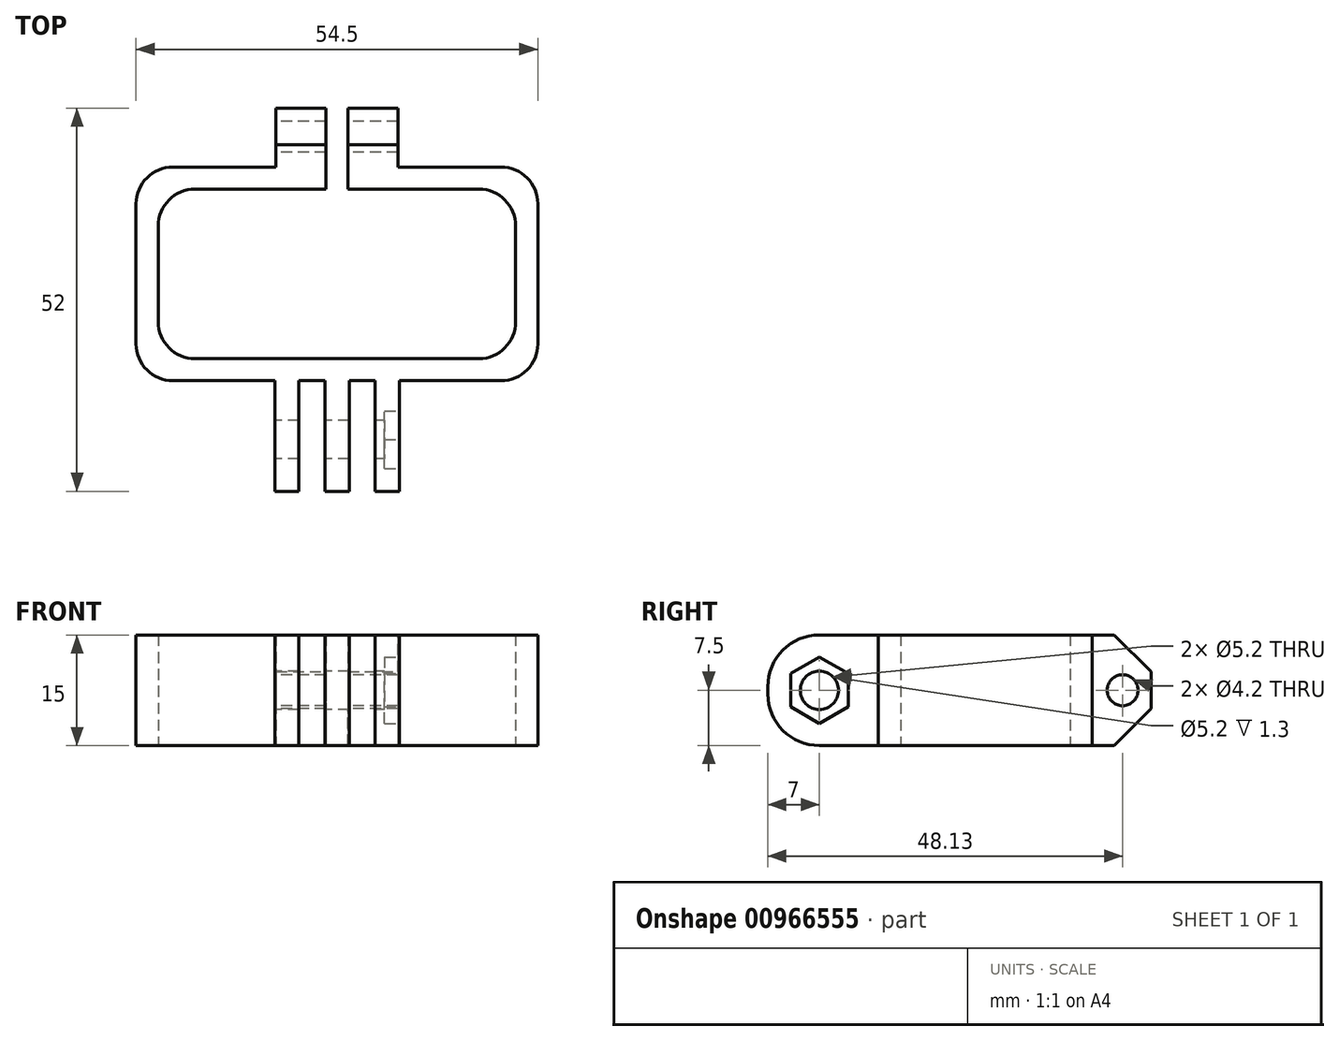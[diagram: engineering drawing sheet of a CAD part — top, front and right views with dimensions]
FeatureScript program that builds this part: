
annotation { "Feature Type Name" : "Feature", "Feature Type Description" : "" }
export const myFeature = defineFeature(function(context is Context, id is Id, definition is map)
    precondition{}
    {
        {
            var Q0;
            Q0=qCreatedBy(makeId("Top.planeOp"),FACE);
            var sketch = newSketch(context, id + "F0", { "sketchPlane" : qUnion([Q0])});
            skLineSegment(sketch, "E0.bottom", {"start": v(22.25, -14.5) * mm, "end": v(8.45, -14.5) * mm});
            skLineSegment(sketch, "E0.top", {"start": v(22.25, 14.5) * mm, "end": v(8.28, 14.5) * mm});
            skLineSegment(sketch, "E0.left", {"start": v(27.25, -9.5) * mm, "end": v(27.25, 9.5) * mm});
            skLineSegment(sketch, "E0.right", {"start": v(-27.25, -9.5) * mm, "end": v(-27.25, 9.5) * mm});
            skPoint(sketch, "E0.middle", {"position": v(0, 0) * mm});
            skLineSegment(sketch, "E1.top", {"start": v(-8.45, -29.5) * mm, "end": v(-5.15, -29.5) * mm});
            skLineSegment(sketch, "E1.left", {"start": v(-8.45, -14.5) * mm, "end": v(-8.45, -29.5) * mm});
            skLineSegment(sketch, "E1.right", {"start": v(-5.15, -14.5) * mm, "end": v(-5.15, -29.5) * mm});
            skLineSegment(sketch, "E2.top", {"start": v(-1.65, -29.5) * mm, "end": v(1.65, -29.5) * mm});
            skLineSegment(sketch, "E2.left", {"start": v(-1.65, -14.5) * mm, "end": v(-1.65, -29.5) * mm});
            skLineSegment(sketch, "E2.right", {"start": v(1.65, -14.5) * mm, "end": v(1.65, -29.5) * mm});
            skLineSegment(sketch, "E3.top", {"start": v(5.15, -29.5) * mm, "end": v(8.45, -29.5) * mm});
            skLineSegment(sketch, "E3.left", {"start": v(5.15, -14.5) * mm, "end": v(5.15, -29.5) * mm});
            skLineSegment(sketch, "E3.right", {"start": v(8.45, -14.5) * mm, "end": v(8.45, -29.5) * mm});
            skLineSegment(sketch, "E4", {"start": v(-5.15, -22.9) * mm, "end": v(-1.65, -22.9) * mm, "construction": true});
            skLineSegment(sketch, "E5", {"start": v(1.65, -22.9) * mm, "end": v(5.15, -22.9) * mm, "construction": true});
            skLineSegment(sketch, "E6.bottom", {"start": v(19.25, -11.5) * mm, "end": v(-19.25, -11.5) * mm});
            skLineSegment(sketch, "E6.top", {"start": v(19.25, 11.5) * mm, "end": v(1.5, 11.5) * mm});
            skLineSegment(sketch, "E6.left", {"start": v(24.25, -6.5) * mm, "end": v(24.25, 6.5) * mm});
            skLineSegment(sketch, "E6.right", {"start": v(-24.25, -6.5) * mm, "end": v(-24.25, 6.5) * mm});
            skLineSegment(sketch, "E7", {"start": v(-1.65, -14.5) * mm, "end": v(1.65, -29.5) * mm, "construction": true});
            skLineSegment(sketch, "E8", {"start": v(1.65, -14.5) * mm, "end": v(-1.65, -29.5) * mm, "construction": true});
            skLineSegment(sketch, "E9", {"start": v(0, 57.59) * mm, "end": v(0, -68.32) * mm, "construction": true});
            skLineSegment(sketch, "E10.trimOffspring", {"start": v(-8.45, -14.5) * mm, "end": v(-22.25, -14.5) * mm});
            skLineSegment(sketch, "E11.trimOffspring", {"start": v(-1.65, -14.5) * mm, "end": v(-5.15, -14.5) * mm});
            skLineSegment(sketch, "E12.trimOffspring", {"start": v(5.15, -14.5) * mm, "end": v(1.65, -14.5) * mm});
            skPoint(sketch, "E13.visualSharp", {"position": v(-24.25, 11.5) * mm});
            skArc(sketch, "E13.filletArc", {"start": v(-19.25, 11.5) * mm, "mid": v(-22.79, 10.04) * mm, "end": v(-24.25, 6.5) * mm});
            skPoint(sketch, "E14.visualSharp", {"position": v(24.25, 11.5) * mm});
            skArc(sketch, "E14.filletArc", {"start": v(24.25, 6.5) * mm, "mid": v(22.79, 10.04) * mm, "end": v(19.25, 11.5) * mm});
            skPoint(sketch, "E15.visualSharp", {"position": v(24.25, -11.5) * mm});
            skArc(sketch, "E15.filletArc", {"start": v(19.25, -11.5) * mm, "mid": v(22.79, -10.04) * mm, "end": v(24.25, -6.5) * mm});
            skPoint(sketch, "E16.visualSharp", {"position": v(-24.25, -11.5) * mm});
            skArc(sketch, "E16.filletArc", {"start": v(-24.25, -6.5) * mm, "mid": v(-22.79, -10.04) * mm, "end": v(-19.25, -11.5) * mm});
            skPoint(sketch, "E17.visualSharp", {"position": v(-27.25, -14.5) * mm});
            skArc(sketch, "E17.filletArc", {"start": v(-27.25, -9.5) * mm, "mid": v(-25.79, -13.04) * mm, "end": v(-22.25, -14.5) * mm});
            skPoint(sketch, "E18.visualSharp", {"position": v(-27.25, 14.5) * mm});
            skArc(sketch, "E18.filletArc", {"start": v(-22.25, 14.5) * mm, "mid": v(-25.79, 13.04) * mm, "end": v(-27.25, 9.5) * mm});
            skPoint(sketch, "E19.visualSharp", {"position": v(27.25, 14.5) * mm});
            skArc(sketch, "E19.filletArc", {"start": v(27.25, 9.5) * mm, "mid": v(25.79, 13.04) * mm, "end": v(22.25, 14.5) * mm});
            skPoint(sketch, "E20.visualSharp", {"position": v(27.25, -14.5) * mm});
            skArc(sketch, "E20.filletArc", {"start": v(22.25, -14.5) * mm, "mid": v(25.79, -13.04) * mm, "end": v(27.25, -9.5) * mm});
            skLineSegment(sketch, "E21.top", {"start": v(8.28, 22.5) * mm, "end": v(1.5, 22.5) * mm});
            skLineSegment(sketch, "E21.left", {"start": v(8.28, 14.5) * mm, "end": v(8.28, 22.5) * mm});
            skLineSegment(sketch, "E21.right", {"start": v(-8.28, 14.5) * mm, "end": v(-8.28, 22.5) * mm});
            skPoint(sketch, "E21.middle", {"position": v(0, 18.5) * mm});
            skLineSegment(sketch, "E22.left", {"start": v(1.5, 14.5) * mm, "end": v(1.5, 22.5) * mm});
            skLineSegment(sketch, "E22.right", {"start": v(-1.5, 14.5) * mm, "end": v(-1.5, 22.5) * mm});
            skLineSegment(sketch, "E23.trimOffspring", {"start": v(-1.5, 22.5) * mm, "end": v(-8.28, 22.5) * mm});
            skLineSegment(sketch, "E24.trimOffspring", {"start": v(-8.28, 14.5) * mm, "end": v(-22.25, 14.5) * mm});
            skLineSegment(sketch, "E25", {"start": v(-1.5, 14.5) * mm, "end": v(-1.5, 11.5) * mm});
            skLineSegment(sketch, "E26", {"start": v(1.5, 14.5) * mm, "end": v(1.5, 11.5) * mm});
            skLineSegment(sketch, "E27.trimOffspring", {"start": v(-1.5, 11.5) * mm, "end": v(-19.25, 11.5) * mm});
            skSolve(sketch);
        }
        {
            var Q0;
            Q0 = qSketchRegion(id + "F0", true);
            extrude(context, id + "F1", {"entities" : qUnion([Q0]), "depth" : 15 * mm, "offsetDistance" : 25 * mm});
        }
        {
            var Q0;
            Q0=makeQuery(id+"F1.opExtrude","CAP_EDGE",EDGE,{"disambiguationData":[OSD([sQuery(id+"F0.wireOp",EDGE,"E1.top")])],"isStart":false});
            var Q1;
            Q1=makeQuery(id+"F1.opExtrude","CAP_EDGE",EDGE,{"disambiguationData":[OSD([sQuery(id+"F0.wireOp",EDGE,"E1.top")])],"isStart":true});
            var Q2;
            Q2=makeQuery(id+"F1.opExtrude","CAP_EDGE",EDGE,{"disambiguationData":[OSD([sQuery(id+"F0.wireOp",EDGE,"E2.top")])],"isStart":false});
            var Q3;
            Q3=makeQuery(id+"F1.opExtrude","CAP_EDGE",EDGE,{"disambiguationData":[OSD([sQuery(id+"F0.wireOp",EDGE,"E3.top")])],"isStart":false});
            var Q4;
            Q4=makeQuery(id+"F1.opExtrude","CAP_EDGE",EDGE,{"disambiguationData":[OSD([sQuery(id+"F0.wireOp",EDGE,"E3.top")])],"isStart":true});
            var Q5;
            Q5=makeQuery(id+"F1.opExtrude","CAP_EDGE",EDGE,{"disambiguationData":[OSD([sQuery(id+"F0.wireOp",EDGE,"E2.top")])],"isStart":true});
            fillet(context, id + "F2", {"entities" : qUnion([Q0, Q1, Q2, Q3, Q4, Q5]), "radius" : 7 * mm, "tangentPropagation" : true, "allowEdgeOverflow" : false});
        }
        {
            var Q0;
            Q0=makeQuery(id+"F1.opExtrude","SWEPT_FACE",FACE,{"disambiguationData":[OSD([sQuery(id+"F0.wireOp",EDGE,"E1.left")])]});
            var sketch = newSketch(context, id + "F3", { "sketchPlane" : qUnion([Q0])});
            skLineSegment(sketch, "E28", {"start": v(29.5, 7.5) * mm, "end": v(-27.74, 7.5) * mm, "construction": true});
            skCircle(sketch, "E29", {"center": v(22.5, 7.5) * mm, "radius": 2.6 * mm});
            skCircle(sketch, "E30", {"center": v(-18.63, 7.5) * mm, "radius": 2.1 * mm});
            skSolve(sketch);
        }
        {
            var Q0;
            Q0 = qSketchRegion(id + "F3", true);
            extrude(context, id + "F4", {"entities" : qUnion([Q0]), "operationType" : NewBodyOperationType.REMOVE, "oppositeDirection" : true, "depth" : 25 * mm, "offsetDistance" : 25 * mm});
        }
        {
            var Q0;
            Q0=makeQuery(id+"F1.opExtrude","SWEPT_FACE",FACE,{"disambiguationData":[OSD([sQuery(id+"F0.wireOp",EDGE,"E3.right")])]});
            var sketch = newSketch(context, id + "F5", { "sketchPlane" : qUnion([Q0])});
            skCircle(sketch, "E31.cCircle", {"center": v(-22.5, 7.5) * mm, "radius": 3.9 * mm, "construction": true});
            skLineSegment(sketch, "E31.0", {"start": v(-18.6, 9.75) * mm, "end": v(-18.6, 5.25) * mm});
            skLineSegment(sketch, "E31.1", {"start": v(-18.6, 5.25) * mm, "end": v(-22.5, 3) * mm});
            skLineSegment(sketch, "E31.2", {"start": v(-22.5, 3) * mm, "end": v(-26.4, 5.25) * mm});
            skLineSegment(sketch, "E31.3", {"start": v(-26.4, 5.25) * mm, "end": v(-26.4, 9.75) * mm});
            skLineSegment(sketch, "E31.4", {"start": v(-26.4, 9.75) * mm, "end": v(-22.5, 12) * mm});
            skLineSegment(sketch, "E31.5", {"start": v(-22.5, 12) * mm, "end": v(-18.6, 9.75) * mm});
            skPoint(sketch, "E31.0.midPoint", {"position": v(-18.6, 7.5) * mm});
            skSolve(sketch);
        }
        {
            var Q0;
            Q0 = qSketchRegion(id + "F5", true);
            extrude(context, id + "F6", {"entities" : qUnion([Q0]), "operationType" : NewBodyOperationType.REMOVE, "oppositeDirection" : true, "depth" : 2 * mm, "offsetDistance" : 25 * mm});
        }
        {
            var Q0;
            Q0=makeQuery(id+"F1.opExtrude","CAP_EDGE",EDGE,{"disambiguationData":[OSD([sQuery(id+"F0.wireOp",EDGE,"E21.top")])],"isStart":false});
            var Q1;
            Q1=makeQuery(id+"F1.opExtrude","CAP_EDGE",EDGE,{"disambiguationData":[OSD([sQuery(id+"F0.wireOp",EDGE,"E23.trimOffspring")])],"isStart":false});
            var Q2;
            Q2=makeQuery(id+"F1.opExtrude","CAP_EDGE",EDGE,{"disambiguationData":[OSD([sQuery(id+"F0.wireOp",EDGE,"E21.top")])],"isStart":true});
            var Q3;
            Q3=makeQuery(id+"F1.opExtrude","CAP_EDGE",EDGE,{"disambiguationData":[OSD([sQuery(id+"F0.wireOp",EDGE,"E23.trimOffspring")])],"isStart":true});
            chamfer(context, id + "F7", {"entities" : qUnion([Q0, Q1, Q2, Q3]), "width" : 5 * mm, "tangentPropagation" : true});
        }
    });
